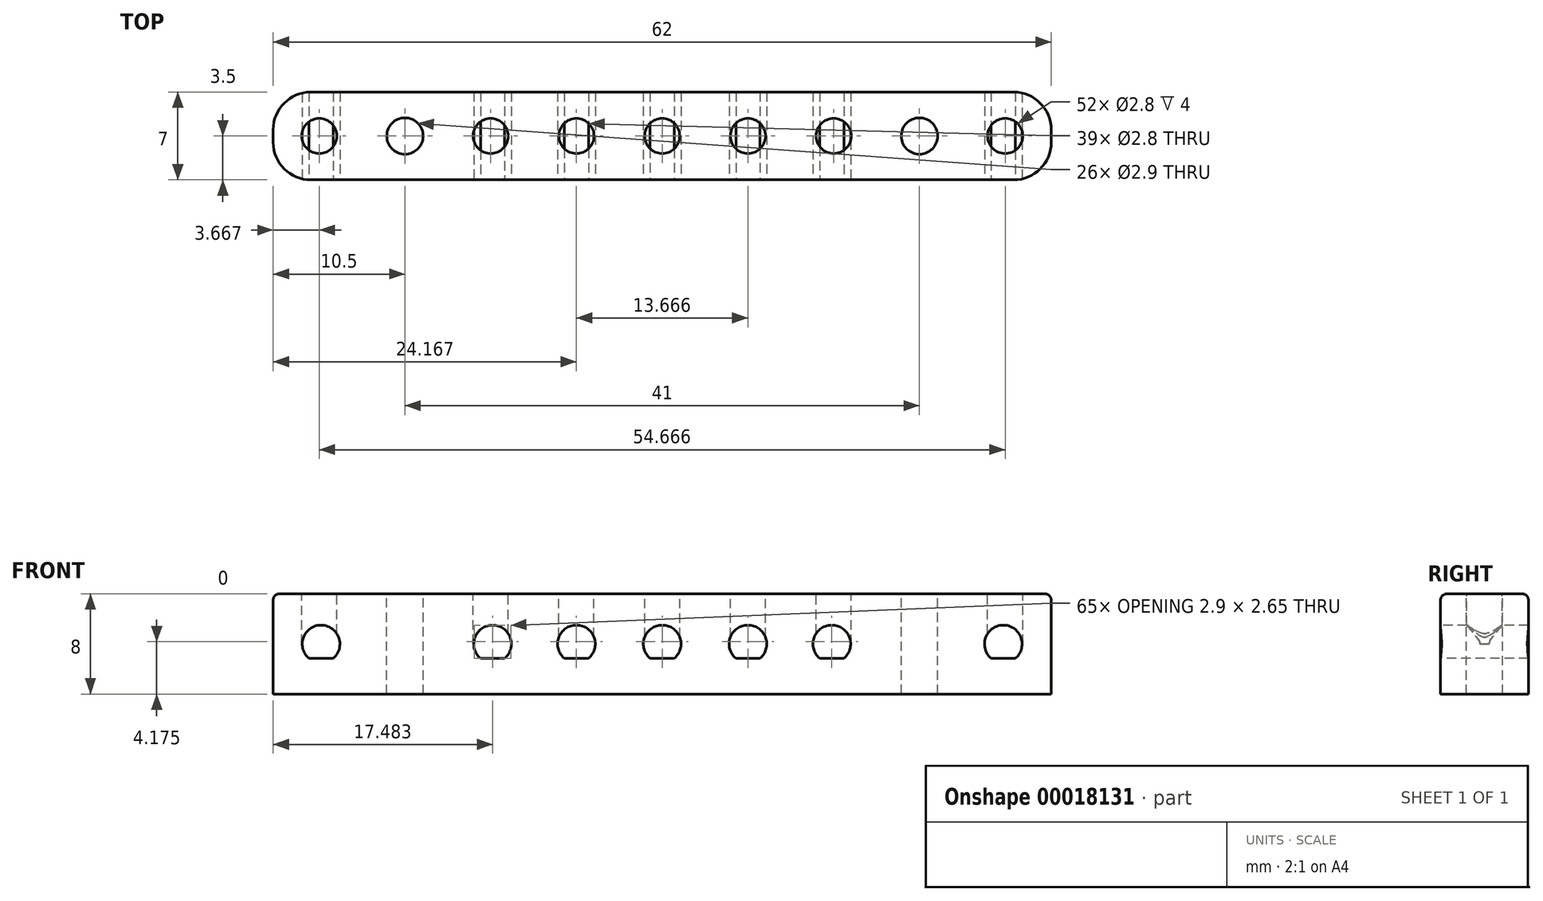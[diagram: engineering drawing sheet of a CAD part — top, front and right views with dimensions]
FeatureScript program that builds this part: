
annotation { "Feature Type Name" : "Feature", "Feature Type Description" : "" }
export const myFeature = defineFeature(function(context is Context, id is Id, definition is map)
    precondition{}
    {
        {
            var Q0;
            Q0=qCreatedBy(makeId("Top.planeOp"),FACE);
            var sketch = newSketch(context, id + "F0", { "sketchPlane" : qUnion([Q0])});
            skLineSegment(sketch, "E0", {"start": v(0, 0) * mm, "end": v(0, 7) * mm});
            skLineSegment(sketch, "E1", {"start": v(0, 7) * mm, "end": v(62, 7) * mm});
            skLineSegment(sketch, "E2", {"start": v(62, 7) * mm, "end": v(62, 0) * mm});
            skLineSegment(sketch, "E3", {"start": v(0, 0) * mm, "end": v(62, 0) * mm});
            skSolve(sketch);
        }
        {
            var Q0;
            {var subQ10=sQuery(id+"F0.wireOp",EDGE,"E0");Q0=makeQuery(id+"F0.imprint","IMPRINT",FACE,{"disambiguationData":[TD([[makeQuery(id+"F0.imprint","IMPRINT",EDGE,{"derivedFrom":subQ10}),-1.0]])]});}
            extrude(context, id + "F1", {"entities" : qUnion([Q0]), "depth" : 8 * mm});
        }
        {
            var Q0;
            Q0=makeQuery(id+"F1.opExtrude","CAP_FACE",FACE,{"disambiguationData":[OSD([sQuery(id+"F0.wireOp",EDGE,"E0"),sQuery(id+"F0.wireOp",EDGE,"E1"),sQuery(id+"F0.wireOp",EDGE,"E2"),sQuery(id+"F0.wireOp",EDGE,"9af4fea9-ab5f-4050-b053-4ace3de3f56e")])],"isStart":false});
            var sketch = newSketch(context, id + "F2", { "sketchPlane" : qUnion([Q0])});
            skLineSegment(sketch, "E4", {"start": v(0, 3.5) * mm, "end": v(62, 3.5) * mm, "construction": true});
            skLineSegment(sketch, "E5", {"start": v(31, 0) * mm, "end": v(31, 7) * mm, "construction": true});
            skCircle(sketch, "E6", {"center": v(10.5, 3.5) * mm, "radius": 1.45 * mm});
            skCircle(sketch, "E7", {"center": v(51.5, 3.5) * mm, "radius": 1.45 * mm});
            skCircle(sketch, "E8", {"center": v(31, 3.5) * mm, "radius": 1.4 * mm});
            skCircle(sketch, "E9", {"center": v(17.33, 3.5) * mm, "radius": 1.4 * mm});
            skCircle(sketch, "E10", {"center": v(24.17, 3.5) * mm, "radius": 1.4 * mm});
            skCircle(sketch, "E11", {"center": v(37.83, 3.5) * mm, "radius": 1.4 * mm});
            skCircle(sketch, "E12", {"center": v(44.67, 3.5) * mm, "radius": 1.4 * mm});
            skCircle(sketch, "E13", {"center": v(58.33, 3.5) * mm, "radius": 1.4 * mm});
            skCircle(sketch, "E14", {"center": v(3.67, 3.5) * mm, "radius": 1.4 * mm});
            skSolve(sketch);
        }
        {
            var Q0;
            Q0=makeQuery(id+"F2.imprint","IMPRINT",FACE,{"disambiguationData":[TD([[makeQuery(id+"F2.imprint","IMPRINT",EDGE,{"derivedFrom":sQuery(id+"F2.wireOp",EDGE,"E6")}),1.0]])]});
            var Q1;
            Q1=makeQuery(id+"F2.imprint","IMPRINT",FACE,{"disambiguationData":[TD([[makeQuery(id+"F2.imprint","IMPRINT",EDGE,{"derivedFrom":sQuery(id+"F2.wireOp",EDGE,"E7")}),1.0]])]});
            extrude(context, id + "F3", {"entities" : qUnion([Q0, Q1]), "operationType" : NewBodyOperationType.REMOVE, "endBound" : BoundingType.THROUGH_ALL, "oppositeDirection" : true, "depth" : 25 * mm});
        }
        {
            var Q0;
            Q0=makeQuery(id+"F2.imprint","IMPRINT",FACE,{"disambiguationData":[TD([[makeQuery(id+"F2.imprint","IMPRINT",EDGE,{"derivedFrom":sQuery(id+"F2.wireOp",EDGE,"E9")}),1.0]])]});
            var Q1;
            Q1=makeQuery(id+"F2.imprint","IMPRINT",FACE,{"disambiguationData":[TD([[makeQuery(id+"F2.imprint","IMPRINT",EDGE,{"derivedFrom":sQuery(id+"F2.wireOp",EDGE,"E14")}),1.0]])]});
            var Q2;
            Q2=makeQuery(id+"F2.imprint","IMPRINT",FACE,{"disambiguationData":[TD([[makeQuery(id+"F2.imprint","IMPRINT",EDGE,{"derivedFrom":sQuery(id+"F2.wireOp",EDGE,"E10")}),1.0]])]});
            var Q3;
            Q3=makeQuery(id+"F2.imprint","IMPRINT",FACE,{"disambiguationData":[TD([[makeQuery(id+"F2.imprint","IMPRINT",EDGE,{"derivedFrom":sQuery(id+"F2.wireOp",EDGE,"E11")}),1.0]])]});
            var Q4;
            Q4=makeQuery(id+"F2.imprint","IMPRINT",FACE,{"disambiguationData":[TD([[makeQuery(id+"F2.imprint","IMPRINT",EDGE,{"derivedFrom":sQuery(id+"F2.wireOp",EDGE,"E12")}),1.0]])]});
            var Q5;
            Q5=makeQuery(id+"F2.imprint","IMPRINT",FACE,{"disambiguationData":[TD([[makeQuery(id+"F2.imprint","IMPRINT",EDGE,{"derivedFrom":sQuery(id+"F2.wireOp",EDGE,"E13")}),1.0]])]});
            var Q6;
            Q6=makeQuery(id+"F2.imprint","IMPRINT",FACE,{"disambiguationData":[TD([[makeQuery(id+"F2.imprint","IMPRINT",EDGE,{"derivedFrom":sQuery(id+"F2.wireOp",EDGE,"E8")}),1.0]])]});
            extrude(context, id + "F4", {"entities" : qUnion([Q0, Q1, Q2, Q3, Q4, Q5, Q6]), "operationType" : NewBodyOperationType.REMOVE, "oppositeDirection" : true, "depth" : 4 * mm});
        }
        {
            var Q0;
            Q0=makeQuery(id+"F1.opExtrude","SWEPT_FACE",FACE,{"disambiguationData":[OSD([sQuery(id+"F0.wireOp",EDGE,"E3")])]});
            var sketch = newSketch(context, id + "F5", { "sketchPlane" : qUnion([Q0])});
            skLineSegment(sketch, "E15", {"start": v(0, 4) * mm, "end": v(62, 4) * mm, "construction": true});
            skLineSegment(sketch, "E16", {"start": v(31, 0) * mm, "end": v(31, 8) * mm, "construction": true});
            skCircle(sketch, "E17", {"center": v(10.65, 4) * mm, "radius": 1.65 * mm, "construction": true});
            skCircle(sketch, "E18", {"center": v(51.35, 4) * mm, "radius": 1.65 * mm, "construction": true});
            skLineSegment(sketch, "E19", {"start": v(2.85, 2.85) * mm, "end": v(4.78, 2.85) * mm});
            skLineSegment(sketch, "E20", {"start": v(4.78, 2.85) * mm, "end": v(16.52, 2.85) * mm, "construction": true});
            skLineSegment(sketch, "E21", {"start": v(57.22, 2.85) * mm, "end": v(59.15, 2.85) * mm});
            skLineSegment(sketch, "E22", {"start": v(45.48, 2.85) * mm, "end": v(57.22, 2.85) * mm, "construction": true});
            skLineSegment(sketch, "E23", {"start": v(43.55, 2.85) * mm, "end": v(45.48, 2.85) * mm});
            skLineSegment(sketch, "E24", {"start": v(38.8, 2.85) * mm, "end": v(43.55, 2.85) * mm, "construction": true});
            skLineSegment(sketch, "E25", {"start": v(36.87, 2.85) * mm, "end": v(38.8, 2.85) * mm});
            skLineSegment(sketch, "E26", {"start": v(31.96, 2.85) * mm, "end": v(36.87, 2.85) * mm, "construction": true});
            skLineSegment(sketch, "E27", {"start": v(30.04, 2.85) * mm, "end": v(31.96, 2.85) * mm});
            skLineSegment(sketch, "E28", {"start": v(25.13, 2.85) * mm, "end": v(30.04, 2.85) * mm, "construction": true});
            skLineSegment(sketch, "E29", {"start": v(23.2, 2.85) * mm, "end": v(25.13, 2.85) * mm});
            skLineSegment(sketch, "E30", {"start": v(18.45, 2.85) * mm, "end": v(23.2, 2.85) * mm, "construction": true});
            skLineSegment(sketch, "E31", {"start": v(16.52, 2.85) * mm, "end": v(18.45, 2.85) * mm});
            skArc(sketch, "E32", {"start": v(2.85, 2.85) * mm, "mid": v(3.82, 2.5) * mm, "end": v(4.78, 2.85) * mm, "construction": true});
            skArc(sketch, "E33", {"start": v(4.78, 2.85) * mm, "mid": v(3.82, 5.5) * mm, "end": v(2.85, 2.85) * mm});
            skArc(sketch, "E34", {"start": v(16.52, 2.85) * mm, "mid": v(17.48, 2.5) * mm, "end": v(18.45, 2.85) * mm, "construction": true});
            skArc(sketch, "E35", {"start": v(18.45, 2.85) * mm, "mid": v(17.48, 5.5) * mm, "end": v(16.52, 2.85) * mm});
            skArc(sketch, "E36", {"start": v(23.2, 2.85) * mm, "mid": v(24.17, 2.5) * mm, "end": v(25.13, 2.85) * mm, "construction": true});
            skArc(sketch, "E37", {"start": v(25.13, 2.85) * mm, "mid": v(24.17, 5.5) * mm, "end": v(23.2, 2.85) * mm});
            skArc(sketch, "E38", {"start": v(30.04, 2.85) * mm, "mid": v(31, 2.5) * mm, "end": v(31.96, 2.85) * mm, "construction": true});
            skArc(sketch, "E39", {"start": v(31.96, 2.85) * mm, "mid": v(31, 5.5) * mm, "end": v(30.04, 2.85) * mm});
            skArc(sketch, "E40", {"start": v(36.87, 2.85) * mm, "mid": v(37.83, 2.5) * mm, "end": v(38.8, 2.85) * mm, "construction": true});
            skArc(sketch, "E41", {"start": v(38.8, 2.85) * mm, "mid": v(37.83, 5.5) * mm, "end": v(36.87, 2.85) * mm});
            skArc(sketch, "E42", {"start": v(43.55, 2.85) * mm, "mid": v(44.52, 2.5) * mm, "end": v(45.48, 2.85) * mm, "construction": true});
            skArc(sketch, "E43", {"start": v(45.48, 2.85) * mm, "mid": v(44.52, 5.5) * mm, "end": v(43.55, 2.85) * mm});
            skArc(sketch, "E44", {"start": v(57.22, 2.85) * mm, "mid": v(58.18, 2.5) * mm, "end": v(59.15, 2.85) * mm, "construction": true});
            skArc(sketch, "E45", {"start": v(59.15, 2.85) * mm, "mid": v(58.18, 5.5) * mm, "end": v(57.22, 2.85) * mm});
            skSolve(sketch);
        }
        {
            var Q0;
            Q0=makeQuery(id+"F5.imprint","IMPRINT",FACE,{"disambiguationData":[TD([[makeQuery(id+"F5.imprint","IMPRINT",EDGE,{"derivedFrom":sQuery(id+"F5.wireOp",EDGE,"E19")}),1.0]])]});
            var Q1;
            Q1=makeQuery(id+"F5.imprint","IMPRINT",FACE,{"disambiguationData":[TD([[makeQuery(id+"F5.imprint","IMPRINT",EDGE,{"derivedFrom":sQuery(id+"F5.wireOp",EDGE,"E31")}),1.0]])]});
            var Q2;
            Q2=makeQuery(id+"F5.imprint","IMPRINT",FACE,{"disambiguationData":[TD([[makeQuery(id+"F5.imprint","IMPRINT",EDGE,{"derivedFrom":sQuery(id+"F5.wireOp",EDGE,"E29")}),1.0]])]});
            var Q3;
            Q3=makeQuery(id+"F5.imprint","IMPRINT",FACE,{"disambiguationData":[TD([[makeQuery(id+"F5.imprint","IMPRINT",EDGE,{"derivedFrom":sQuery(id+"F5.wireOp",EDGE,"E27")}),1.0]])]});
            var Q4;
            Q4=makeQuery(id+"F5.imprint","IMPRINT",FACE,{"disambiguationData":[TD([[makeQuery(id+"F5.imprint","IMPRINT",EDGE,{"derivedFrom":sQuery(id+"F5.wireOp",EDGE,"E25")}),1.0]])]});
            var Q5;
            Q5=makeQuery(id+"F5.imprint","IMPRINT",FACE,{"disambiguationData":[TD([[makeQuery(id+"F5.imprint","IMPRINT",EDGE,{"derivedFrom":sQuery(id+"F5.wireOp",EDGE,"E23")}),1.0]])]});
            var Q6;
            Q6=makeQuery(id+"F5.imprint","IMPRINT",FACE,{"disambiguationData":[TD([[makeQuery(id+"F5.imprint","IMPRINT",EDGE,{"derivedFrom":sQuery(id+"F5.wireOp",EDGE,"E21")}),1.0]])]});
            extrude(context, id + "F6", {"entities" : qUnion([Q0, Q1, Q2, Q3, Q4, Q5, Q6]), "operationType" : NewBodyOperationType.REMOVE, "endBound" : BoundingType.THROUGH_ALL, "oppositeDirection" : true, "depth" : 25 * mm});
        }
        {
            var Q0;
            Q0=makeQuery(id+"F1.opExtrude","CAP_EDGE",EDGE,{"disambiguationData":[OSD([sQuery(id+"F0.wireOp",EDGE,"E3")])],"isStart":false});
            var Q1;
            Q1=makeQuery(id+"F1.opExtrude","CAP_EDGE",EDGE,{"disambiguationData":[OSD([sQuery(id+"F0.wireOp",EDGE,"E1")])],"isStart":false});
            var Q2;
            Q2=makeQuery(id+"F1.opExtrude","CAP_EDGE",EDGE,{"disambiguationData":[OSD([sQuery(id+"F0.wireOp",EDGE,"E2")])],"isStart":false});
            var Q3;
            Q3=makeQuery(id+"F1.opExtrude","CAP_EDGE",EDGE,{"disambiguationData":[OSD([sQuery(id+"F0.wireOp",EDGE,"E0")])],"isStart":false});
            fillet(context, id + "F7", {"entities" : qUnion([Q0, Q1, Q2, Q3]), "radius" : 0.5 * mm, "tangentPropagation" : true, "allowEdgeOverflow" : false});
        }
        {
            var Q0;
            Q0=makeQuery(id+"F1.opExtrude","SWEPT_EDGE",EDGE,{"disambiguationData":[OSD([sQuery(id+"F0.wireOp",EDGE,"E0"),sQuery(id+"F0.wireOp",EDGE,"E3")])]});
            var Q1;
            Q1=makeQuery(id+"F1.opExtrude","SWEPT_EDGE",EDGE,{"disambiguationData":[OSD([sQuery(id+"F0.wireOp",EDGE,"E0"),sQuery(id+"F0.wireOp",EDGE,"E1")])]});
            var Q2;
            Q2=makeQuery(id+"F1.opExtrude","SWEPT_EDGE",EDGE,{"disambiguationData":[OSD([sQuery(id+"F0.wireOp",EDGE,"E2"),sQuery(id+"F0.wireOp",EDGE,"E3")])]});
            var Q3;
            Q3=makeQuery(id+"F1.opExtrude","SWEPT_EDGE",EDGE,{"disambiguationData":[OSD([sQuery(id+"F0.wireOp",EDGE,"E1"),sQuery(id+"F0.wireOp",EDGE,"E2")])]});
            fillet(context, id + "F8", {"entities" : qUnion([Q0, Q1, Q2, Q3]), "radius" : 3 * mm, "tangentPropagation" : true, "allowEdgeOverflow" : false});
        }
    });
